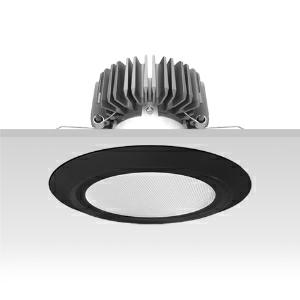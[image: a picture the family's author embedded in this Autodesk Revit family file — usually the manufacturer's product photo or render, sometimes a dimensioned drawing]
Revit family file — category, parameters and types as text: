
# Revit family: 3f_filippi_-_3f_reno_bianco_ampio_3f_filippi_-_30675_a01049_-_3f_reno_200_wh_2000-930_dali_wide___smp_bk_2a22
name_source: partatom
category: Lighting Fixtures
units: mm (PartAtom-declared; Revit-internal decimal feet)

## family parameters
Cut with Voids When Loaded = No
Host = Face
Light Source = No
Part Type = Normal
Room Calculation Point = No
Round Connector Dimension = Use Diameter
Shared = No

## types (1)
- 3F Filippi - 3F Reno Bianco Ampio (1 x LED, 1650 lm, 24 W, 3000 K)
    Apparent Load = 24 VA
    Approval mark = CE
    CIE Flux Codes = 74 92 98 100 100
    Color Rendering = 90
    Color Temperature = 3000 K
    Control Gear = Electronic transformer
    Default Elevation = 1800 mm
    Description = ILLUMINOTECHNICAL
Luminous efficiency 100% (DLOR 100%, ULOR 0%).
Initial luminous flux of the luminaire 1650 lm.
Direct symmetric wide distribution.
Installation Interdistance Transv.D = 1.06 x hu - Long.D = 1.04 x hu.
Average luminance <3000 cd/m² for radial angles >65°.
Tabular UGR (CIE 117 - 4H-8H; S=0.25H; 70/50/20): RUG 21.3 - 21.1.
Beam angle: 70° - 69°.
Luminous efficacy 69 lm/W.
Lifetime (L90/B10): 30000 h. (tq+25°C)
Lifetime (L85/B10): 50000 h. (tq+25°C)
Lifetime (L70/B10): 80000 h. (tq+25°C)
Sudden decreased luminous flux after 50000 hours: 0% (C0).
Photobiological safety in compliance with IEC/TR 62778: RG0 risk exempt, (IEC 62471).
In compliance with IEC/EN 62722-2-1 - IEC/EN 62717 standards.

SOURCE
Compact LED module 2000/930.
Energy efficiency class (UE 2019/2020 - UE 2019/2015): E.
CIE 13.3 Colour rendering index: CRI >90 (R9 >50%).
IES TM-30 Fidelity Index: Rf = 92 Rg = 101.
CCT nominal colour temperature 3000 K.
Colour initial tolerance (MacAdam): SDCM 3.
Zhaga Book 3 compliant.

MECHANICAL
Passive heat dissipator in die-casting aluminium, oversized, for optimum thermal management of the LED module.
Parabolic element with graduated/concentric rings in white polycarbonate.
Transparent external lens with glossy and satin differentiated surfaces, with a cooling and anti-insect system in methacrylate (PMMA).
Fastening spring clips in stainless steel.
Dimensions: diameter 226 mm, height 146 mm. Weight 1.04 kg.
IP44 protection degree for exposed part, IP20 for recessed part.
Mechanical strength to impacts IK05 (0.7 joule).
Glow-wire test resistance 650°C.

ELECTRICAL
Wiring on a separate unit.
Halogen Free DALI-2 DATI (Parts 251, 252, 253), PUSH-DIM, electronic wiring 230V-50/60Hz, power factor 0.95 at full load, THD <25%, constant output current, SELV, class II, 1 driver, 1 DALI addresse.
Power of the luminaire 24 W.
ENEC - CE.
SAFE FLICKER: PstLM=<1 and SVM=<0.4 (IEC TR 61547-1 and IEC TR 63158), to ensure a more comfortable and safe light.
Luminaire compliant with EN 60598-2-22 for power supply from a centralised emergency system CPSS (Central Power Supply System), not incorporated in the luminaire - high risk areas excluded. The default power and flux are 100% in AC and 100% in DC.
Ambient temperature from 0°C to +25°C.
Temperature class T6 max 85°C.
Relative humidity UR: <85%.

INSTALLATION
Pull-up recessed fitting.
False ceiling carving: 200 mm.
All accessories dedicated to this product are available on the Catalog and on our website www.3F-Filippi.com.

ACCESSORIES
A01049 - Anti-glare microprismatic SMP diffuser in methacrylate (PMMA), locked and in line with the trim, in black polycarbonate.

APPLICATIONS
Suitable product for food production plants (HACCP), IFS (Food Version 6), BRC (GSFS Food Version 7).
Environments: architectural, commercial, exhibition areas, transit areas, corridors, shops, display windows, service areas.
In false ceilings with narrow voids.

LIGHT MANAGEMENT
Recommended minimum setting: 10%.
The luminaire, equipped with (DALI-2 DATI) driver, can be controlled manually with 3F Easy Dim technology or automatically/manually with wired or wireless DALI/D2D control systems.
The D2D driver guarantees interoperability with other devices with the same certification by making the following information available:
Device Data (Part 251), Energy Report (Part 252), Diagnosis & Maintenance (Part 253).
In electrical systems without a regulation system (manual or automatic) and DALI bus, a suitable jumper must be made on the DA-DA terminals of the appliance.

WARNING
Luminaire designed for disposal/recycling at end-of-life.
Replaceable (LED only) light source by a professional. Replaceable control gear by a professional.
    Height = 0 mm  [stored 0 ft]
    Lamp = 1 x LED
    Lamp Light Flux = 1650 lm
    Lamp Power = 24 W
    Lamp count = 1
    Length = 226 mm
    Lifetime = 50000 h
    Luminous efficacy = 69 lm/W
    Manufacturer = 3F Filippi
    ModVariant = No
    Model = 3F Filippi - 30675+A01049 - 3F Reno 200 WH 2000-930 DALI WIDE + SMP BK
    Mounting Place = Ceiling
    Mounting Type = Recessed
    Number of Poles = 1
    OnlyDefault = Yes
    Power Factor = 1
    Product Name = 3F Filippi - 3F Reno Bianco Ampio
    Product group = recessed luminaire
    ProductGroupID = 4
    Protection Class = Protection class II
    Protection Degree = IP 20
    RLX_Detail_Level = 1
    RLX_Emergency_Light_Flux = 0 lm
    RLX_Emergency_Type = 0
    RLX_Emergency_Type_DB = No
    RlxData = <blob elided: 100561 chars, md5=763b9cf6>
    Socket = socket
    Standby Power = 0 W
    System Light Flux = 1650 lm
    System Power = 24 W
    Type Comments = Product without accessories
    Type Image = 3ffilippi_3f_reno_200_bk_vs_smp.jpg
    URL = http://relux.com
    VarID = ---
    Voltage = 0 V
    Weight = 0.00 kg
    Width = 0 mm  [stored 0 ft]

note: [stored X ft] marks values corroborated as IEEE doubles in the binary element streams (Revit-internal decimal feet)

## geometry (parser evidence)
native form markers: Blend x4, Sweep x9
no freeform markers — native parametric forms only
